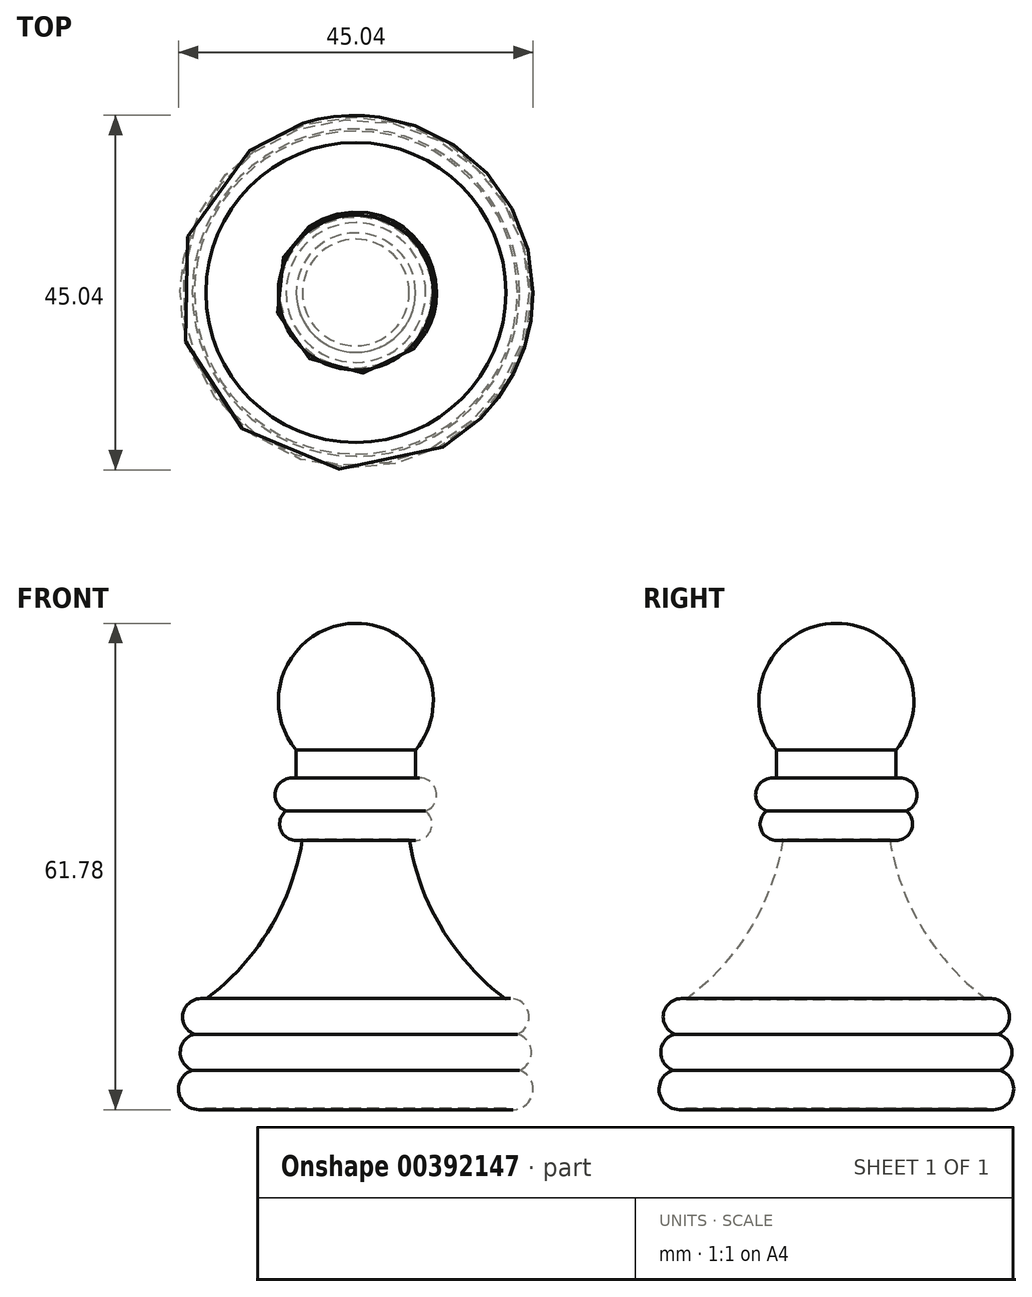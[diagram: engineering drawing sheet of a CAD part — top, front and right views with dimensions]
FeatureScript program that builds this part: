
annotation { "Feature Type Name" : "Feature", "Feature Type Description" : "" }
export const myFeature = defineFeature(function(context is Context, id is Id, definition is map)
    precondition{}
    {
        {
            var Q0;
            Q0=qCreatedBy(makeId("Front.planeOp"),FACE);
            var sketch = newSketch(context, id + "F0", { "sketchPlane" : qUnion([Q0])});
            skLineSegment(sketch, "E0", {"start": v(0, 12.73) * mm, "end": v(0, -38.07) * mm});
            skLineSegment(sketch, "E1", {"start": v(0, -38.07) * mm, "end": v(-19.05, -38.07) * mm});
            skArc(sketch, "E2", {"start": v(-19.05, -33.23) * mm, "mid": v(-22.52, -35.65) * mm, "end": v(-19.05, -38.07) * mm});
            skArc(sketch, "E3", {"start": v(-19.05, -28.71) * mm, "mid": v(-22.31, -30.97) * mm, "end": v(-19.05, -33.23) * mm});
            skArc(sketch, "E4", {"start": v(-19.05, -24.2) * mm, "mid": v(-22, -26.45) * mm, "end": v(-19.05, -28.71) * mm});
            skArc(sketch, "E5", {"start": v(-19.05, -24.2) * mm, "mid": v(-10.93, -15.23) * mm, "end": v(-6.78, -3.87) * mm});
            skArc(sketch, "E6", {"start": v(-6.78, 0) * mm, "mid": v(-9.68, -1.94) * mm, "end": v(-6.78, -3.87) * mm});
            skArc(sketch, "E7", {"start": v(-7.58, 3.87) * mm, "mid": v(-10.21, 1.3) * mm, "end": v(-6.78, 0) * mm});
            skArc(sketch, "E8", {"start": v(0, 23.55) * mm, "mid": v(-8.9, 17.9) * mm, "end": v(-7.58, 7.44) * mm});
            skLineSegment(sketch, "E9", {"start": v(0, 12.73) * mm, "end": v(0, 23.55) * mm});
            skLineSegment(sketch, "E10", {"start": v(-7.58, 3.87) * mm, "end": v(-7.58, 7.44) * mm});
            skPoint(sketch, "E11.orphan", {"position": v(0, 3.87) * mm});
            skSolve(sketch);
        }
        {
            var Q0;
            Q0=qSketchRegion(id+"F0",true);
            var Q1;
            Q1=sQuery(id+"F0.wireOp",EDGE,"E0");
            revolve(context, id + "F1", {"entities" : qUnion([Q0]), "axis" : qUnion([Q1]), "revolveType" : RevolveType.FULL});
        }
        {
            var Q0;
            Q0=qSketchRegion(id+"F0",true);
            var Q1;
            Q1=sQuery(id+"F0.wireOp",EDGE,"E0");
            revolve(context, id + "F2", {"entities" : qUnion([Q0]), "axis" : qUnion([Q1]), "revolveType" : RevolveType.FULL});
        }
    });
